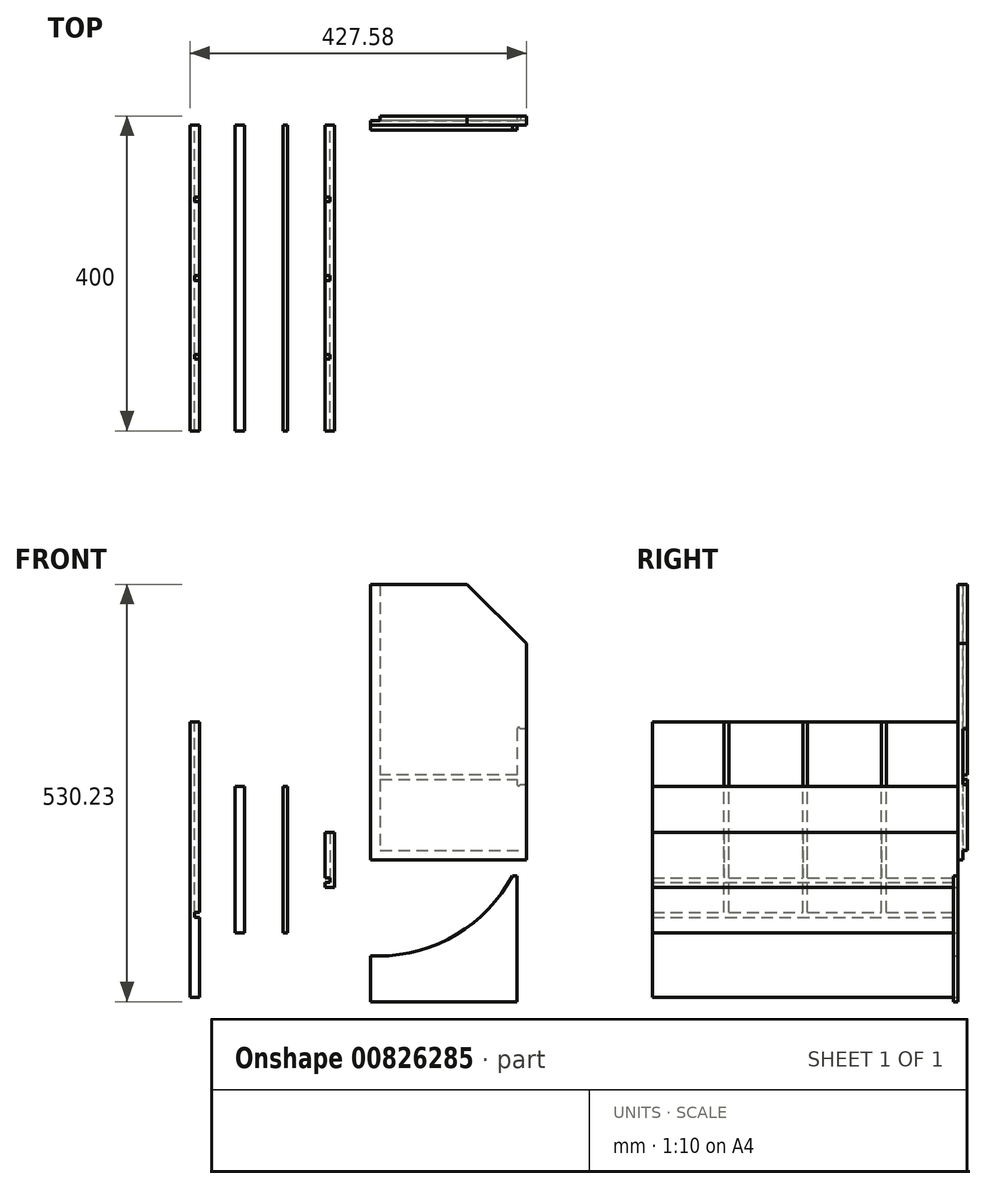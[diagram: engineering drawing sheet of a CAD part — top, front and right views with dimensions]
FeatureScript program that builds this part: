
annotation { "Feature Type Name" : "Feature", "Feature Type Description" : "" }
export const myFeature = defineFeature(function(context is Context, id is Id, definition is map)
    precondition{}
    {
        {
            assignVariable(context, id + "F0", {"name" : "plyWidthMM", "anyValue" : 12});
        }
        {
            assignVariable(context, id + "F1", {"name" : "trolleyWidthMM", "anyValue" : 400});
        }
        {
            assignVariable(context, id + "F2", {"name" : "thinPlyWidthMM", "anyValue" : 6});
        }
        {
            var Q0;
            Q0=qCreatedBy(makeId("Front.planeOp"),FACE);
            var sketch = newSketch(context, id + "F3", { "sketchPlane" : qUnion([Q0])});
            skLineSegment(sketch, "E0", {"start": v(0, 0) * mm, "end": v(0, 350) * mm});
            skLineSegment(sketch, "E1", {"start": v(0, 350) * mm, "end": v(122.53, 350) * mm});
            skLineSegment(sketch, "E2", {"start": v(122.53, 350) * mm, "end": v(198, 274.53) * mm});
            skLineSegment(sketch, "E3", {"start": v(198, 274.53) * mm, "end": v(198, 0) * mm});
            skLineSegment(sketch, "E4", {"start": v(198, 0) * mm, "end": v(0, 0) * mm});
            skCircle(sketch, "E5", {"center": v(102, 198) * mm, "radius": 90 * mm, "construction": true});
            skLineSegment(sketch, "E6", {"start": v(186, 108) * mm, "end": v(12, 108) * mm});
            skLineSegment(sketch, "E7", {"start": v(12, 102) * mm, "end": v(186, 102) * mm});
            skLineSegment(sketch, "E8", {"start": v(12, 350) * mm, "end": v(12, 108) * mm});
            skLineSegment(sketch, "E9", {"start": v(12, 12) * mm, "end": v(198, 12) * mm});
            skLineSegment(sketch, "E10", {"start": v(198, 166) * mm, "end": v(190, 166) * mm});
            skLineSegment(sketch, "E11", {"start": v(186, 166) * mm, "end": v(186, 108) * mm});
            skLineSegment(sketch, "E12.trimOffspring", {"start": v(12, 102) * mm, "end": v(12, 12) * mm});
            skArc(sketch, "E13", {"start": v(186, 166) * mm, "mid": v(188, 168) * mm, "end": v(190, 166) * mm});
            skLineSegment(sketch, "E14", {"start": v(186, 102) * mm, "end": v(186, 96) * mm});
            skArc(sketch, "E15", {"start": v(186, 96) * mm, "mid": v(188, 94) * mm, "end": v(190, 96) * mm});
            skLineSegment(sketch, "E16.trimOffspring", {"start": v(190, 96) * mm, "end": v(198, 96) * mm});
            skSolve(sketch);
        }
        {
            var Q0;
            {var subQ4=sQuery(id+"F3.wireOp",EDGE,"E0");Q0=makeQuery(id+"F3.imprint","IMPRINT",FACE,{"disambiguationData":[TD([[makeQuery(id+"F3.imprint","IMPRINT",EDGE,{"derivedFrom":subQ4}),-1.0]])]});}
            extrude(context, id + "F4", {"entities" : qUnion([Q0]), "oppositeDirection" : true, "depth" : (getVariable(context, 'plyWidthMM') / 2) * mm, "offsetDistance" : 25 * mm});
        }
        {
            var Q0;
            {var subQ1=sQuery(id+"F3.wireOp",EDGE,"E2");Q0=makeQuery(id+"F3.imprint","IMPRINT",FACE,{"disambiguationData":[TD([[makeQuery(id+"F3.imprint","IMPRINT",EDGE,{"derivedFrom":subQ1}),-1.0]])]});}
            var Q1;
            {var subQ0=sQuery(id+"F3.wireOp",EDGE,"E7");Q1=makeQuery(id+"F3.imprint","IMPRINT",FACE,{"disambiguationData":[TD([[makeQuery(id+"F3.imprint","IMPRINT",EDGE,{"derivedFrom":subQ0}),-1.0]])]});}
            extrude(context, id + "F5", {"entities" : qUnion([Q0, Q1]), "operationType" : NewBodyOperationType.ADD, "oppositeDirection" : true, "depth" : (getVariable(context, 'plyWidthMM')) * mm, "offsetDistance" : 25 * mm});
        }
        {
            var Q0;
            Q0=qCreatedBy(makeId("Front.planeOp"),FACE);
            var sketch = newSketch(context, id + "F6", { "sketchPlane" : qUnion([Q0])});
            skLineSegment(sketch, "E17.bottom", {"start": v(-57.87, 35) * mm, "end": v(-45.87, 35) * mm});
            skLineSegment(sketch, "E17.top", {"start": v(-57.87, -35) * mm, "end": v(-45.87, -35) * mm});
            skLineSegment(sketch, "E17.left", {"start": v(-57.87, 35) * mm, "end": v(-57.87, -35) * mm});
            skLineSegment(sketch, "E17.right", {"start": v(-45.87, 35) * mm, "end": v(-45.87, -35) * mm});
            skPoint(sketch, "E17.middle", {"position": v(-51.87, 0) * mm});
            skLineSegment(sketch, "E18.bottom", {"start": v(-111.48, -93) * mm, "end": v(-105.48, -93) * mm});
            skLineSegment(sketch, "E18.top", {"start": v(-111.48, 93) * mm, "end": v(-105.48, 93) * mm});
            skLineSegment(sketch, "E18.left", {"start": v(-111.48, -93) * mm, "end": v(-111.48, 93) * mm});
            skLineSegment(sketch, "E18.right", {"start": v(-105.48, -93) * mm, "end": v(-105.48, 93) * mm});
            skPoint(sketch, "E18.middle", {"position": v(-108.48, 0) * mm});
            skLineSegment(sketch, "E19.bottom", {"start": v(-217.58, -175) * mm, "end": v(-229.58, -175) * mm});
            skLineSegment(sketch, "E19.top", {"start": v(-217.58, 175) * mm, "end": v(-229.58, 175) * mm});
            skLineSegment(sketch, "E19.left", {"start": v(-217.58, -175) * mm, "end": v(-217.58, 175) * mm});
            skLineSegment(sketch, "E19.right", {"start": v(-229.58, -175) * mm, "end": v(-229.58, 175) * mm});
            skPoint(sketch, "E19.middle", {"position": v(-223.58, 0) * mm});
            skLineSegment(sketch, "E20.bottom", {"start": v(-160.25, -93) * mm, "end": v(-172.25, -93) * mm});
            skLineSegment(sketch, "E20.top", {"start": v(-160.25, 93) * mm, "end": v(-172.25, 93) * mm});
            skLineSegment(sketch, "E20.left", {"start": v(-160.25, -93) * mm, "end": v(-160.25, 93) * mm});
            skLineSegment(sketch, "E20.right", {"start": v(-172.25, -93) * mm, "end": v(-172.25, 93) * mm});
            skPoint(sketch, "E20.middle", {"position": v(-166.25, 0) * mm});
            skLineSegment(sketch, "E21", {"start": v(-229.58, -67) * mm, "end": v(-223.58, -67) * mm, "construction": true});
            skLineSegment(sketch, "E22", {"start": v(-223.58, -67) * mm, "end": v(-223.58, -73) * mm});
            skLineSegment(sketch, "E23", {"start": v(-223.58, -67) * mm, "end": v(-217.58, -67) * mm});
            skLineSegment(sketch, "E24", {"start": v(-57.87, -23) * mm, "end": v(-51.87, -23) * mm});
            skLineSegment(sketch, "E25", {"start": v(-51.87, -23) * mm, "end": v(-51.87, -29) * mm});
            skLineSegment(sketch, "E26", {"start": v(-51.87, -29) * mm, "end": v(-57.87, -29) * mm});
            skLineSegment(sketch, "E27", {"start": v(-51.87, -23) * mm, "end": v(-45.87, -23) * mm, "construction": true});
            skLineSegment(sketch, "E28", {"start": v(-223.58, -73) * mm, "end": v(-217.58, -73) * mm});
            skSolve(sketch);
        }
        {
            var Q0;
            Q0=makeQuery(id+"F6.imprint","IMPRINT",FACE,{"disambiguationData":[TD([[makeQuery(id+"F6.imprint","IMPRINT",EDGE,{"derivedFrom":sQuery(id+"F6.wireOp",EDGE,"E17.bottom")}),-1.0]])]});
            var Q1;
            Q1=makeQuery(id+"F6.imprint","IMPRINT",FACE,{"disambiguationData":[TD([[makeQuery(id+"F6.imprint","IMPRINT",EDGE,{"derivedFrom":sQuery(id+"F6.wireOp",EDGE,"E18.bottom")}),1.0]])]});
            var Q2;
            Q2=makeQuery(id+"F6.imprint","IMPRINT",FACE,{"disambiguationData":[TD([[makeQuery(id+"F6.imprint","IMPRINT",EDGE,{"derivedFrom":sQuery(id+"F6.wireOp",EDGE,"E19.bottom")}),-1.0]])]});
            var Q3;
            Q3=makeQuery(id+"F6.imprint","IMPRINT",FACE,{"disambiguationData":[TD([[makeQuery(id+"F6.imprint","IMPRINT",EDGE,{"derivedFrom":sQuery(id+"F6.wireOp",EDGE,"E20.bottom")}),-1.0]])]});
            var Q4;
            Q4 = qConstructionFilter(qBodyType(qCreatedBy(id + "F6" ,EDGE), BodyType.WIRE), ConstructionObject.NO);
            extrude(context, id + "F7", {"entities" : qUnion([Q0, Q1, Q2, Q3]), "surfaceEntities" : qUnion([Q4]), "depth" : (getVariable(context, 'trolleyWidthMM') - getVariable(context, 'plyWidthMM')) * mm, "offsetDistance" : 25 * mm});
        }
        {
            var Q0;
            {var subQ0=sQuery(id+"F6.wireOp",EDGE,"E19.left");Q0=makeQuery(id+"F7.opExtrude","SWEPT_FACE",FACE,{"disambiguationData":[OSD([subQ0]),TDD([makeQuery(id+"F6.imprint","IMPRINT",EDGE,{"disambiguationData":[TD([[makeQuery(id+"F6.imprint","INTERSECT",VERTEX,{"derivedFrom":[sQuery(id+"F6.wireOp",EDGE,"E19.top"),subQ0]}),1.0]])],"derivedFrom":subQ0})])]});}
            var sketch = newSketch(context, id + "F8", { "sketchPlane" : qUnion([Q0])});
            skLineSegment(sketch, "E29.bottom", {"start": v(-197, -67) * mm, "end": v(-191, -67) * mm});
            skLineSegment(sketch, "E29.top", {"start": v(-197, 175) * mm, "end": v(-191, 175) * mm});
            skLineSegment(sketch, "E29.left", {"start": v(-197, -67) * mm, "end": v(-197, 175) * mm});
            skLineSegment(sketch, "E29.right", {"start": v(-191, -67) * mm, "end": v(-191, 175) * mm});
            skLineSegment(sketch, "E30.bottom", {"start": v(-297, -67) * mm, "end": v(-291, -67) * mm});
            skLineSegment(sketch, "E30.top", {"start": v(-297, 175) * mm, "end": v(-291, 175) * mm});
            skLineSegment(sketch, "E30.left", {"start": v(-297, -67) * mm, "end": v(-297, 175) * mm});
            skLineSegment(sketch, "E30.right", {"start": v(-291, -67) * mm, "end": v(-291, 175) * mm});
            skLineSegment(sketch, "E31.bottom", {"start": v(-97, -67) * mm, "end": v(-91, -67) * mm});
            skLineSegment(sketch, "E31.top", {"start": v(-97, 175) * mm, "end": v(-91, 175) * mm});
            skLineSegment(sketch, "E31.left", {"start": v(-97, -67) * mm, "end": v(-97, 175) * mm});
            skLineSegment(sketch, "E31.right", {"start": v(-91, -67) * mm, "end": v(-91, 175) * mm});
            skSolve(sketch);
        }
        {
            var Q0;
            Q0 = qSketchRegion(id + "F8", true);
            extrude(context, id + "F9", {"entities" : qUnion([Q0]), "operationType" : NewBodyOperationType.REMOVE, "oppositeDirection" : true, "depth" : (getVariable(context, 'plyWidthMM') / 2) * mm, "offsetDistance" : 25 * mm});
        }
        {
            var Q0;
            {var subQ0=sQuery(id+"F6.wireOp",EDGE,"E17.left");Q0=makeQuery(id+"F7.opExtrude","SWEPT_FACE",FACE,{"disambiguationData":[OSD([subQ0]),TDD([makeQuery(id+"F6.imprint","IMPRINT",EDGE,{"disambiguationData":[TD([[makeQuery(id+"F6.imprint","INTERSECT",VERTEX,{"derivedFrom":[sQuery(id+"F6.wireOp",EDGE,"E17.bottom"),subQ0]}),-1.0]])],"derivedFrom":subQ0})])]});}
            var sketch = newSketch(context, id + "F10", { "sketchPlane" : qUnion([Q0])});
            skLineSegment(sketch, "E32.0.0", {"start": v(297, -67) * mm, "end": v(291, -67) * mm});
            skLineSegment(sketch, "E32.0.1", {"start": v(291, -67) * mm, "end": v(291, 175) * mm});
            skLineSegment(sketch, "E32.0.2", {"start": v(291, 175) * mm, "end": v(297, 175) * mm});
            skLineSegment(sketch, "E32.0.3", {"start": v(297, 175) * mm, "end": v(297, -67) * mm});
            skLineSegment(sketch, "E33.0.0", {"start": v(197, -67) * mm, "end": v(191, -67) * mm});
            skLineSegment(sketch, "E33.0.1", {"start": v(191, -67) * mm, "end": v(191, 175) * mm});
            skLineSegment(sketch, "E33.0.2", {"start": v(191, 175) * mm, "end": v(197, 175) * mm});
            skLineSegment(sketch, "E33.0.3", {"start": v(197, 175) * mm, "end": v(197, -67) * mm});
            skLineSegment(sketch, "E34.0.0", {"start": v(97, -67) * mm, "end": v(91, -67) * mm});
            skLineSegment(sketch, "E34.0.1", {"start": v(91, -67) * mm, "end": v(91, 175) * mm});
            skLineSegment(sketch, "E34.0.2", {"start": v(91, 175) * mm, "end": v(97, 175) * mm});
            skLineSegment(sketch, "E34.0.3", {"start": v(97, 175) * mm, "end": v(97, -67) * mm});
            skSolve(sketch);
        }
        {
            var Q0;
            {var subQ0=sQuery(id+"F10.wireOp",EDGE,"E33.0.1");var subQ1=sQuery(id+"F6.wireOp",EDGE,"E17.left");var subQ2=makeQuery(id+"F7.opExtrude","SWEPT_EDGE",EDGE,{"disambiguationData":[OSD([subQ1,sQuery(id+"F6.wireOp",EDGE,"E24")])]});var subQ3=makeQuery(id+"F10.imprint","INTERSECT",VERTEX,{"derivedFrom":[subQ2,subQ0]});Q0=makeQuery(id+"F10.imprint","IMPRINT",FACE,{"disambiguationData":[TD([[makeQuery(id+"F10.imprint","IMPRINT",EDGE,{"disambiguationData":[TD([[subQ3,-1.0]])],"derivedFrom":subQ0}),-1.0]])]});}
            var Q1;
            {var subQ0=sQuery(id+"F10.wireOp",EDGE,"E32.0.1");var subQ1=sQuery(id+"F6.wireOp",EDGE,"E17.left");var subQ2=makeQuery(id+"F7.opExtrude","SWEPT_EDGE",EDGE,{"disambiguationData":[OSD([subQ1,sQuery(id+"F6.wireOp",EDGE,"E24")])]});var subQ3=makeQuery(id+"F10.imprint","INTERSECT",VERTEX,{"derivedFrom":[subQ2,subQ0]});Q1=makeQuery(id+"F10.imprint","IMPRINT",FACE,{"disambiguationData":[TD([[makeQuery(id+"F10.imprint","IMPRINT",EDGE,{"disambiguationData":[TD([[subQ3,-1.0]])],"derivedFrom":subQ0}),-1.0]])]});}
            var Q2;
            {var subQ0=sQuery(id+"F10.wireOp",EDGE,"E34.0.1");var subQ1=sQuery(id+"F6.wireOp",EDGE,"E17.left");var subQ2=makeQuery(id+"F7.opExtrude","SWEPT_EDGE",EDGE,{"disambiguationData":[OSD([subQ1,sQuery(id+"F6.wireOp",EDGE,"E24")])]});var subQ3=makeQuery(id+"F10.imprint","INTERSECT",VERTEX,{"derivedFrom":[subQ2,subQ0]});Q2=makeQuery(id+"F10.imprint","IMPRINT",FACE,{"disambiguationData":[TD([[makeQuery(id+"F10.imprint","IMPRINT",EDGE,{"disambiguationData":[TD([[subQ3,-1.0]])],"derivedFrom":subQ0}),-1.0]])]});}
            extrude(context, id + "F11", {"entities" : qUnion([Q0, Q1, Q2]), "operationType" : NewBodyOperationType.REMOVE, "oppositeDirection" : true, "depth" : (getVariable(context, 'plyWidthMM') / 2) * mm, "offsetDistance" : 25 * mm});
        }
        {
            var Q0;
            Q0=qCreatedBy(makeId("Front.planeOp"),FACE);
            var sketch = newSketch(context, id + "F12", { "sketchPlane" : qUnion([Q0])});
            skLineSegment(sketch, "E35", {"start": v(0, -122.23) * mm, "end": v(0, -180.23) * mm});
            skLineSegment(sketch, "E36", {"start": v(0, -180.23) * mm, "end": v(186, -180.23) * mm});
            skLineSegment(sketch, "E37", {"start": v(186, -180.23) * mm, "end": v(186, -20.23) * mm});
            skLineSegment(sketch, "E38", {"start": v(186, -20.23) * mm, "end": v(180, -20.23) * mm});
            skLineSegment(sketch, "E39", {"start": v(0, -122.23) * mm, "end": v(10, -122.23) * mm});
            skArc(sketch, "E40", {"start": v(10, -122.23) * mm, "mid": v(109.13, -94.78) * mm, "end": v(180, -20.23) * mm});
            skSolve(sketch);
        }
        {
            var Q0;
            Q0=makeQuery(id+"F12.imprint","IMPRINT",FACE,{"disambiguationData":[TD([[makeQuery(id+"F12.imprint","IMPRINT",EDGE,{"derivedFrom":sQuery(id+"F12.wireOp",EDGE,"E35")}),1.0]])]});
            extrude(context, id + "F13", {"entities" : qUnion([Q0]), "depth" : (getVariable(context, 'thinPlyWidthMM')) * mm, "offsetDistance" : 25 * mm});
        }
    });
